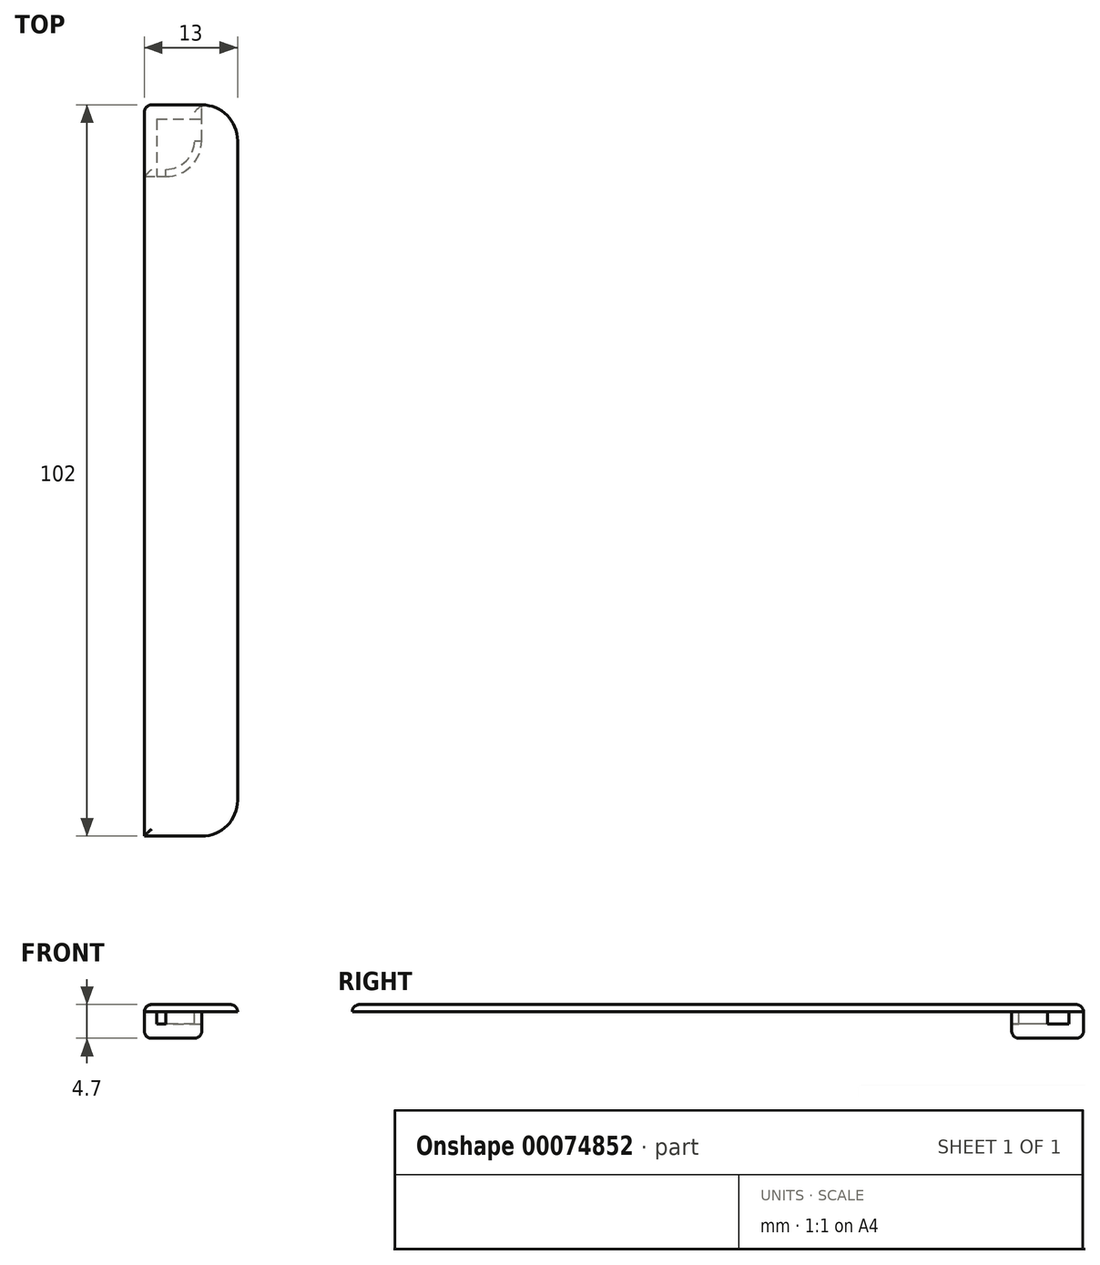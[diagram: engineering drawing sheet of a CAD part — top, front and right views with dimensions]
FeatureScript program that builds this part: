
annotation { "Feature Type Name" : "Feature", "Feature Type Description" : "" }
export const myFeature = defineFeature(function(context is Context, id is Id, definition is map)
    precondition{}
    {
        {
            var Q0;
            Q0=qCreatedBy(makeId("Top.planeOp"),FACE);
            var sketch = newSketch(context, id + "F0", { "sketchPlane" : qUnion([Q0])});
            skLineSegment(sketch, "E0.bottom", {"start": v(6.5, -51) * mm, "end": v(-6.5, -51) * mm});
            skLineSegment(sketch, "E0.top", {"start": v(1.5, 51) * mm, "end": v(-6.5, 51) * mm});
            skLineSegment(sketch, "E0.left", {"start": v(6.5, -51) * mm, "end": v(6.5, 46) * mm});
            skLineSegment(sketch, "E0.right", {"start": v(-6.5, -51) * mm, "end": v(-6.5, 51) * mm});
            skPoint(sketch, "E0.middle", {"position": v(0, 0) * mm});
            skPoint(sketch, "E1.visualSharp", {"position": v(6.5, 51) * mm});
            skArc(sketch, "E1.filletArc", {"start": v(6.5, 46) * mm, "mid": v(5.04, 49.54) * mm, "end": v(1.5, 51) * mm});
            skSolve(sketch);
        }
        {
            var Q0;
            Q0 = qSketchRegion(id + "F0", true);
            extrude(context, id + "F1", {"entities" : qUnion([Q0]), "depth" : 1 * mm});
        }
        {
            var Q0;
            Q0=makeQuery(id+"F1.opExtrude","CAP_FACE",FACE,{"disambiguationData":[OSD([sQuery(id+"F0.wireOp",EDGE,"E0.bottom"),sQuery(id+"F0.wireOp",EDGE,"E0.top"),sQuery(id+"F0.wireOp",EDGE,"E0.left"),sQuery(id+"F0.wireOp",EDGE,"E0.right"),sQuery(id+"F0.wireOp",EDGE,"E1.filletArc")])],"isStart":true});
            var sketch = newSketch(context, id + "F2", { "sketchPlane" : qUnion([Q0])});
            skLineSegment(sketch, "E2.bottom", {"start": v(-6.5, -51) * mm, "end": v(1.5, -51) * mm});
            skLineSegment(sketch, "E2.top", {"start": v(-6.5, -49) * mm, "end": v(1.5, -49) * mm});
            skLineSegment(sketch, "E2.left", {"start": v(-6.5, -49) * mm, "end": v(-6.5, -51) * mm});
            skLineSegment(sketch, "E2.right", {"start": v(1.5, -49) * mm, "end": v(1.5, -51) * mm});
            skLineSegment(sketch, "E3.bottom", {"start": v(-6.5, -51) * mm, "end": v(-4.8, -51) * mm});
            skLineSegment(sketch, "E3.top", {"start": v(-6.5, -41) * mm, "end": v(-4.8, -41) * mm});
            skLineSegment(sketch, "E3.left", {"start": v(-6.5, -51) * mm, "end": v(-6.5, -41) * mm});
            skLineSegment(sketch, "E3.right", {"start": v(-4.8, -51) * mm, "end": v(-4.8, -41) * mm});
            skSolve(sketch);
        }
        {
            var Q0;
            Q0 = qSketchRegion(id + "F2", true);
            extrude(context, id + "F3", {"entities" : qUnion([Q0]), "operationType" : NewBodyOperationType.ADD, "depth" : 1.7 * mm});
        }
        {
            var Q0;
            Q0=makeQuery(id+"F3.opExtrude","CAP_FACE",FACE,{"disambiguationData":[OSD([sQuery(id+"F2.wireOp",EDGE,"E2.bottom"),sQuery(id+"F2.wireOp",EDGE,"E2.top"),sQuery(id+"F2.wireOp",EDGE,"E2.right"),sQuery(id+"F2.wireOp",EDGE,"E3.bottom"),sQuery(id+"F2.wireOp",EDGE,"E3.top"),sQuery(id+"F2.wireOp",EDGE,"E3.left"),sQuery(id+"F2.wireOp",EDGE,"E3.right")])],"isStart":false});
            var sketch = newSketch(context, id + "F4", { "sketchPlane" : qUnion([Q0])});
            skLineSegment(sketch, "E4.bottom", {"start": v(1.5, -51) * mm, "end": v(-6.5, -51) * mm});
            skLineSegment(sketch, "E4.top", {"start": v(1.5, -41) * mm, "end": v(-6.5, -41) * mm});
            skLineSegment(sketch, "E4.left", {"start": v(1.5, -51) * mm, "end": v(1.5, -41) * mm});
            skLineSegment(sketch, "E4.right", {"start": v(-6.5, -51) * mm, "end": v(-6.5, -41) * mm});
            skSolve(sketch);
        }
        {
            var Q0;
            Q0 = qSketchRegion(id + "F4", true);
            extrude(context, id + "F5", {"entities" : qUnion([Q0]), "operationType" : NewBodyOperationType.ADD, "depth" : 2 * mm});
        }
        {
            var Q0;
            Q0=makeQuery(id+"F1.opExtrude","SWEPT_EDGE",EDGE,{"disambiguationData":[OSD([sQuery(id+"F0.wireOp",EDGE,"E0.bottom"),sQuery(id+"F0.wireOp",EDGE,"E0.left")])]});
            var Q1;
            Q1=makeQuery(id+"F5.opExtrude","SWEPT_EDGE",EDGE,{"disambiguationData":[OSD([sQuery(id+"F4.wireOp",EDGE,"E4.top"),sQuery(id+"F4.wireOp",EDGE,"E4.left")])]});
            fillet(context, id + "F6", {"entities" : qUnion([Q0, Q1]), "radius" : 5 * mm, "tangentPropagation" : true, "allowEdgeOverflow" : false});
        }
        {
            var Q0;
            Q0=makeQuery(id+"F1.opExtrude","CAP_FACE",FACE,{"disambiguationData":[OSD([sQuery(id+"F0.wireOp",EDGE,"E0.bottom"),sQuery(id+"F0.wireOp",EDGE,"E0.top"),sQuery(id+"F0.wireOp",EDGE,"E0.left"),sQuery(id+"F0.wireOp",EDGE,"E0.right"),sQuery(id+"F0.wireOp",EDGE,"E1.filletArc")])],"isStart":false});
            fillet(context, id + "F7", {"entities" : qUnion([Q0]), "radius" : 1 * mm, "tangentPropagation" : true, "allowEdgeOverflow" : false});
        }
        {
            var Q0;
            Q0=makeQuery(id+"F5.boolean.opBoolean","MERGE",EDGE,{"derivedFrom":[makeQuery(id+"F3.boolean.opBoolean","MERGE",EDGE,{"derivedFrom":[makeQuery(id+"F1.opExtrude","SWEPT_EDGE",EDGE,{"disambiguationData":[OSD([sQuery(id+"F0.wireOp",EDGE,"E0.top"),sQuery(id+"F0.wireOp",EDGE,"E0.right")])]}),makeQuery(id+"F3.opExtrude","SWEPT_EDGE",EDGE,{"disambiguationData":[OSD([sQuery(id+"F2.wireOp",EDGE,"E3.bottom"),sQuery(id+"F2.wireOp",EDGE,"E3.left")])]})]}),makeQuery(id+"F5.opExtrude","SWEPT_EDGE",EDGE,{"disambiguationData":[OSD([sQuery(id+"F4.wireOp",EDGE,"E4.bottom"),sQuery(id+"F4.wireOp",EDGE,"E4.right")])]})]});
            var Q1;
            Q1=makeQuery(id+"F5.opExtrude","CAP_FACE",FACE,{"disambiguationData":[OSD([sQuery(id+"F4.wireOp",EDGE,"E4.bottom"),sQuery(id+"F4.wireOp",EDGE,"E4.top"),sQuery(id+"F4.wireOp",EDGE,"E4.left"),sQuery(id+"F4.wireOp",EDGE,"E4.right")])],"isStart":false});
            fillet(context, id + "F8", {"entities" : qUnion([Q0, Q1]), "radius" : 1 * mm, "tangentPropagation" : true, "allowEdgeOverflow" : false});
        }
        {
            var Q0;
            Q0=makeQuery(id+"F1.opExtrude","CAP_FACE",FACE,{"disambiguationData":[OSD([sQuery(id+"F0.wireOp",EDGE,"E0.bottom"),sQuery(id+"F0.wireOp",EDGE,"E0.top"),sQuery(id+"F0.wireOp",EDGE,"E0.left"),sQuery(id+"F0.wireOp",EDGE,"E0.right"),sQuery(id+"F0.wireOp",EDGE,"E1.filletArc")])],"isStart":true});
            var sketch = newSketch(context, id + "F9", { "sketchPlane" : qUnion([Q0])});
            skLineSegment(sketch, "E5.0.0", {"start": v(0.5, -46) * mm, "end": v(1.5, -46) * mm});
            skArc(sketch, "E5.0.1", {"start": v(-3.5, -41) * mm, "mid": v(0.04, -42.46) * mm, "end": v(1.5, -46) * mm});
            skLineSegment(sketch, "E5.0.2", {"start": v(-3.5, -41) * mm, "end": v(-3.5, -42) * mm});
            skArc(sketch, "E5.0.3", {"start": v(-3.5, -42) * mm, "mid": v(-0.67, -43.17) * mm, "end": v(0.5, -46) * mm});
            skSolve(sketch);
        }
        {
            var Q0;
            Q0 = qSketchRegion(id + "F9", true);
            extrude(context, id + "F10", {"entities" : qUnion([Q0]), "operationType" : NewBodyOperationType.ADD, "endBound" : BoundingType.UP_TO_NEXT, "depth" : 25 * mm});
        }
    });
